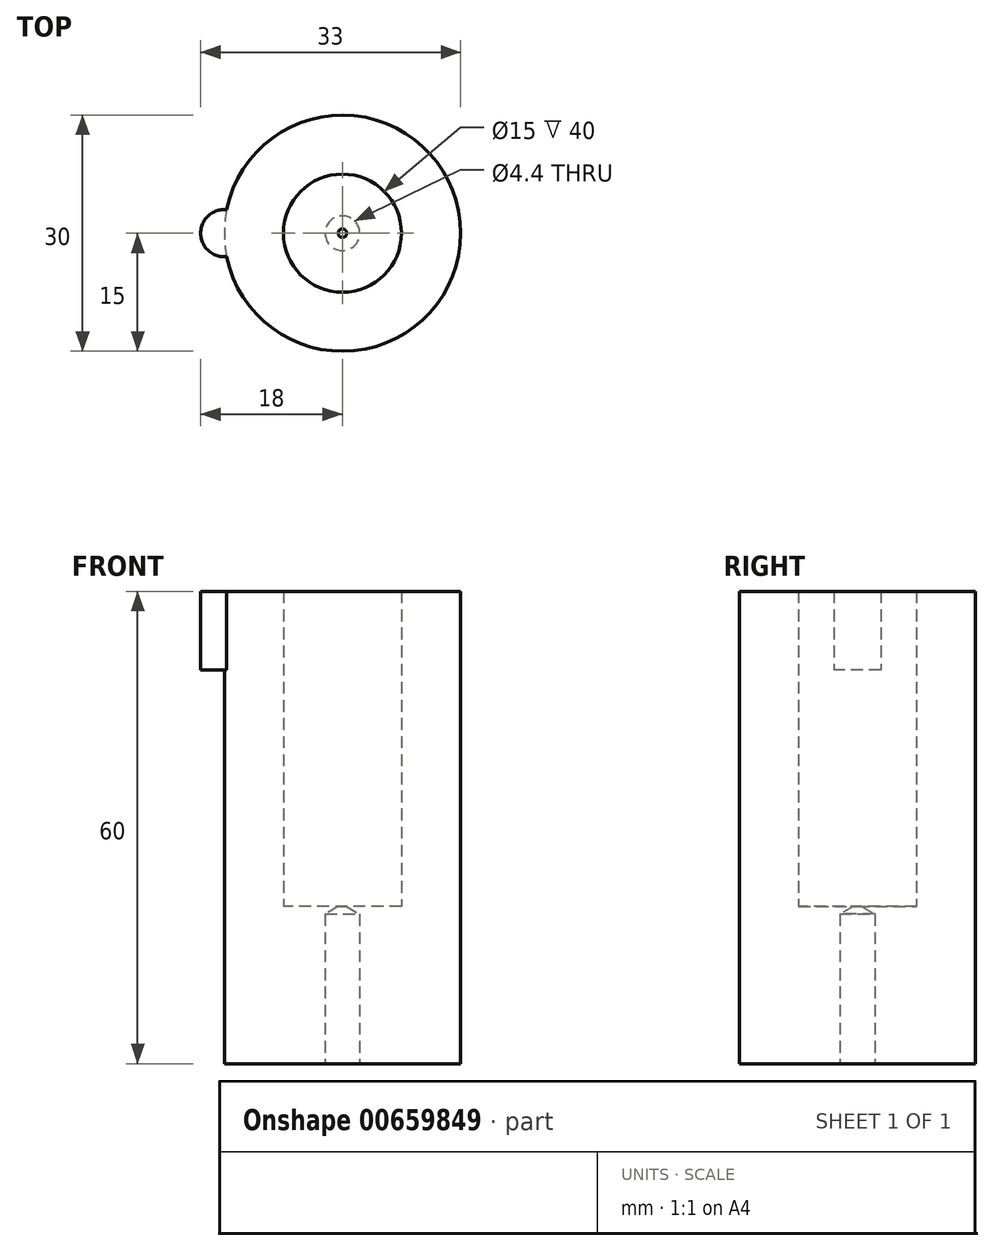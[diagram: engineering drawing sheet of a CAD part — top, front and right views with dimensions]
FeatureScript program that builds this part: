
annotation { "Feature Type Name" : "Feature", "Feature Type Description" : "" }
export const myFeature = defineFeature(function(context is Context, id is Id, definition is map)
    precondition{}
    {
        {
            var Q0;
            Q0=qCreatedBy(makeId("Top.planeOp"),FACE);
            var sketch = newSketch(context, id + "F0", { "sketchPlane" : qUnion([Q0])});
            skCircle(sketch, "E0", {"center": v(0, 0) * mm, "radius": 15 * mm});
            skPoint(sketch, "E1", {"position": v(-15, 0) * mm});
            skPoint(sketch, "E2", {"position": v(15, 0) * mm});
            skArc(sketch, "E3", {"start": v(14.7, 2.98) * mm, "mid": v(18, 0) * mm, "end": v(14.7, -2.98) * mm});
            skArc(sketch, "E4", {"start": v(-14.7, 2.98) * mm, "mid": v(-18, 0) * mm, "end": v(-14.7, -2.98) * mm});
            skCircle(sketch, "E5", {"center": v(0, 0) * mm, "radius": 7.5 * mm});
            skSolve(sketch);
        }
        {
            var Q0;
            Q0=makeQuery(id+"F0.imprint","IMPRINT",FACE,{"disambiguationData":[TD([[makeQuery(id+"F0.imprint","IMPRINT",EDGE,{"derivedFrom":sQuery(id+"F0.wireOp",EDGE,"E5")}),-1.0]])]});
            extrude(context, id + "F1", {"entities" : qUnion([Q0]), "depth" : 40 * mm, "offsetDistance" : 25 * mm});
        }
        {
            var Q0;
            {var subQ0=sQuery(id+"F0.wireOp",EDGE,"E4");Q0=makeQuery(id+"F0.imprint","IMPRINT",FACE,{"disambiguationData":[TD([[makeQuery(id+"F0.imprint","IMPRINT",EDGE,{"derivedFrom":subQ0}),1.0]])]});}
            var Q1;
            {var subQ0=sQuery(id+"F0.wireOp",EDGE,"E3");Q1=makeQuery(id+"F0.imprint","IMPRINT",FACE,{"disambiguationData":[TD([[makeQuery(id+"F0.imprint","IMPRINT",EDGE,{"derivedFrom":subQ0}),-1.0]])]});}
            extrude(context, id + "F2", {"entities" : qUnion([Q0, Q1]), "operationType" : NewBodyOperationType.ADD, "depth" : 40 * mm, "offsetDistance" : 25 * mm, "hasSecondDirection" : true, "secondDirectionOppositeDirection" : true, "secondDirectionDepth" : -30 * mm});
        }
        {
            var Q0;
            Q0=makeQuery(id+"F1.opExtrude","CAP_FACE",FACE,{"disambiguationData":[OSD([sQuery(id+"F0.wireOp",EDGE,"E0"),sQuery(id+"F0.wireOp",EDGE,"E5")])],"isStart":true});
            var sketch = newSketch(context, id + "F3", { "sketchPlane" : qUnion([Q0])});
            skCircle(sketch, "E6", {"center": v(0, 0) * mm, "radius": 15 * mm});
            skSolve(sketch);
        }
        {
            var Q0;
            Q0 = qSketchRegion(id + "F3", true);
            extrude(context, id + "F4", {"entities" : qUnion([Q0]), "operationType" : NewBodyOperationType.ADD, "depth" : 20 * mm, "offsetDistance" : 25 * mm});
        }
        {
            var Q0;
            Q0=makeQuery(id+"F4.opExtrude","CAP_FACE",FACE,{"disambiguationData":[OSD([sQuery(id+"F3.wireOp",EDGE,"E6")])],"isStart":false});
            var sketch = newSketch(context, id + "F5", { "sketchPlane" : qUnion([Q0])});
            skPoint(sketch, "E7", {"position": v(0, 0) * mm});
            skSolve(sketch);
        }
        {
            var Q0;
            Q0=sQuery(id+"F5.wireOp",VERTEX,"E7");
            var Q1;
            Q1=makeQuery(id+"F1.opExtrude","SWEPT_BODY",BODY,{"disambiguationData":[OSD([sQuery(id+"F0.wireOp",EDGE,"E0"),sQuery(id+"F0.wireOp",EDGE,"E5")])]});
            hole(context, id + "F6", {"style" : HoleStyle.SIMPLE, "endStyle" : HoleEndStyle.BLIND, "standardTappedOrClearance" : lookupTablePath({ "standard" : "ISO", "fit" : "Normal", "size" : "M4", "type" : "Clearance" }), "standardBlindInLast" : lookupTablePath({ "fit" : "Standard", "standard" : "ISO", "size" : "M4", "type" : "Clearance" }), "holeDiameter" : 4.4 * mm, "majorDiameter" : 5 * mm, "holeDepth" : 19 * mm, "isTappedThrough" : true, "tappedDepth" : 12 * mm, "tapClearance" : 3, "locations" : qUnion([Q0]), "scope" : qUnion([Q1])});
        }
    });
